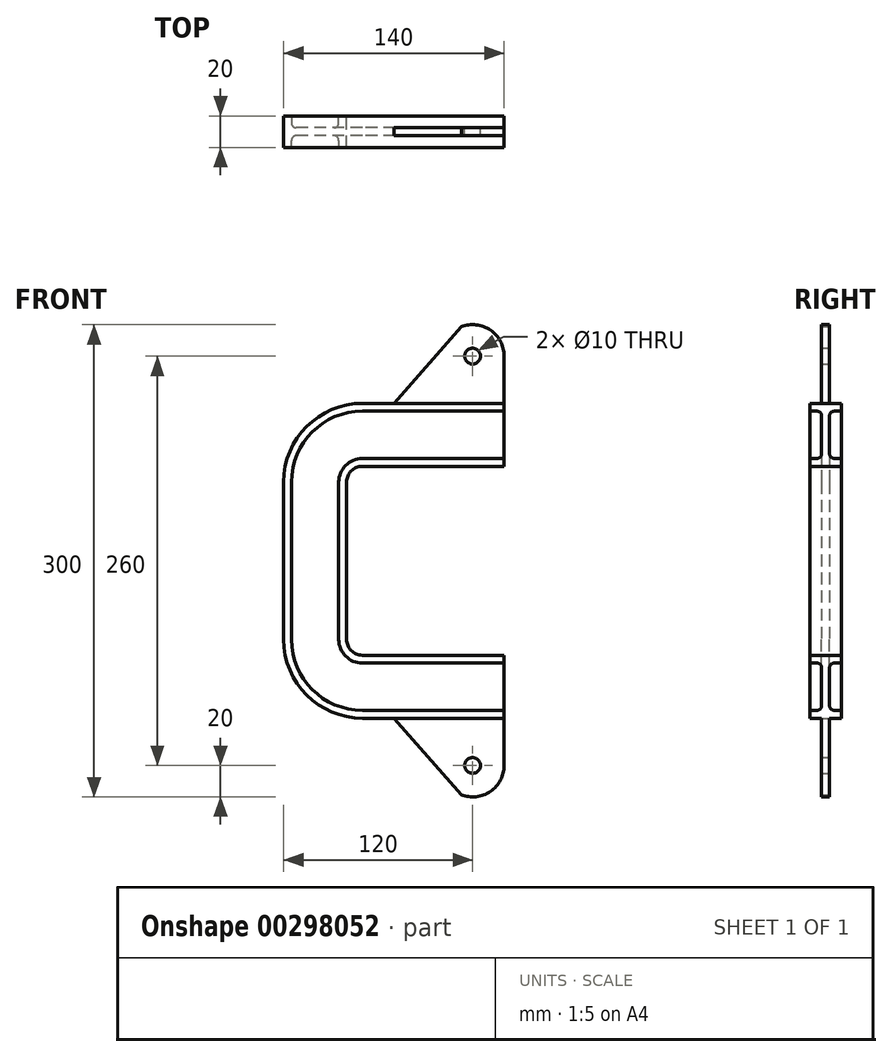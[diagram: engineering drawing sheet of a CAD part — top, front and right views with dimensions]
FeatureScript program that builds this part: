
annotation { "Feature Type Name" : "Feature", "Feature Type Description" : "" }
export const myFeature = defineFeature(function(context is Context, id is Id, definition is map)
    precondition{}
    {
        {
            var Q0;
            Q0=qCreatedBy(makeId("Front.planeOp"),FACE);
            var sketch = newSketch(context, id + "F0", { "sketchPlane" : qUnion([Q0])});
            skLineSegment(sketch, "E0", {"start": v(-100, 0) * mm, "end": v(-100, 50) * mm});
            skLineSegment(sketch, "E1", {"start": v(-90, 60) * mm, "end": v(0, 60) * mm});
            skPoint(sketch, "E2.visualSharp", {"position": v(-100, 60) * mm});
            skArc(sketch, "E2.filletArc", {"start": v(-90, 60) * mm, "mid": v(-97.07, 57.07) * mm, "end": v(-100, 50) * mm});
            skSolve(sketch);
        }
        {
            var Q0;
            Q0=qCreatedBy(makeId("Right.planeOp"),FACE);
            var sketch = newSketch(context, id + "F1", { "sketchPlane" : qUnion([Q0])});
            skLineSegment(sketch, "E3", {"start": v(0, 100) * mm, "end": v(10, 100) * mm});
            skLineSegment(sketch, "E4", {"start": v(10, 100) * mm, "end": v(10, 95) * mm});
            skLineSegment(sketch, "E5", {"start": v(10, 95) * mm, "end": v(5.5, 95) * mm});
            skLineSegment(sketch, "E6", {"start": v(2.5, 92) * mm, "end": v(2.5, 68) * mm});
            skLineSegment(sketch, "E7", {"start": v(5.5, 65) * mm, "end": v(10, 65) * mm});
            skLineSegment(sketch, "E8", {"start": v(10, 65) * mm, "end": v(10, 60) * mm});
            skLineSegment(sketch, "E9", {"start": v(10, 60) * mm, "end": v(0, 60) * mm});
            skPoint(sketch, "E10.visualSharp", {"position": v(2.5, 95) * mm});
            skArc(sketch, "E10.filletArc", {"start": v(5.5, 95) * mm, "mid": v(3.38, 94.12) * mm, "end": v(2.5, 92) * mm});
            skPoint(sketch, "E11.visualSharp", {"position": v(2.5, 65) * mm});
            skArc(sketch, "E11.filletArc", {"start": v(2.5, 68) * mm, "mid": v(3.38, 65.88) * mm, "end": v(5.5, 65) * mm});
            skLineSegment(sketch, "E12.MirrorCS", {"start": v(-5.5, 65) * mm, "end": v(-10, 65) * mm});
            skLineSegment(sketch, "E13.MirrorCS", {"start": v(-10, 95) * mm, "end": v(-5.5, 95) * mm});
            skArc(sketch, "E14.MirrorCS", {"start": v(-2.5, 68) * mm, "mid": v(-3.38, 65.88) * mm, "end": v(-5.5, 65) * mm});
            skArc(sketch, "E15.MirrorCS", {"start": v(-5.5, 95) * mm, "mid": v(-3.38, 94.12) * mm, "end": v(-2.5, 92) * mm});
            skLineSegment(sketch, "E16.MirrorCS", {"start": v(0, 100) * mm, "end": v(-10, 100) * mm});
            skLineSegment(sketch, "E17.MirrorCS", {"start": v(-10, 100) * mm, "end": v(-10, 95) * mm});
            skLineSegment(sketch, "E18.MirrorCS", {"start": v(-2.5, 92) * mm, "end": v(-2.5, 68) * mm});
            skLineSegment(sketch, "E19.MirrorCS", {"start": v(-10, 65) * mm, "end": v(-10, 60) * mm});
            skPoint(sketch, "E20.MirrorP", {"position": v(-2.5, 95) * mm});
            skLineSegment(sketch, "E21.MirrorCS", {"start": v(-10, 60) * mm, "end": v(0, 60) * mm});
            skPoint(sketch, "E22.MirrorP", {"position": v(-2.5, 65) * mm});
            skSolve(sketch);
        }
        {
            var Q0;
            Q0=makeQuery(id+"F1.imprint","IMPRINT",FACE,{"disambiguationData":[TD([[makeQuery(id+"F1.imprint","IMPRINT",EDGE,{"derivedFrom":sQuery(id+"F1.wireOp",EDGE,"E3")}),-1.0]])]});
            var Q1;
            Q1=sQuery(id+"F0.wireOp",EDGE,"E1");
            var Q2;
            Q2=sQuery(id+"F0.wireOp",EDGE,"E2.filletArc");
            var Q3;
            Q3=sQuery(id+"F0.wireOp",EDGE,"E0");
            sweep(context, id + "F2", {"profiles" : qUnion([Q0]), "path" : qUnion([Q1, Q2, Q3])});
        }
        {
            var Q0;
            Q0=makeQuery(id+"F2.opSweep","SWEPT_BODY",BODY,{"disambiguationData":[OSD([sQuery(id+"F0.wireOp",EDGE,"E0"),sQuery(id+"F1.wireOp",EDGE,"E3"),sQuery(id+"F1.wireOp",EDGE,"E4"),sQuery(id+"F1.wireOp",EDGE,"E5"),sQuery(id+"F1.wireOp",EDGE,"E6"),sQuery(id+"F1.wireOp",EDGE,"E7"),sQuery(id+"F1.wireOp",EDGE,"E8"),sQuery(id+"F1.wireOp",EDGE,"E9"),sQuery(id+"F1.wireOp",EDGE,"E10.filletArc"),sQuery(id+"F1.wireOp",EDGE,"E11.filletArc"),sQuery(id+"F1.wireOp",EDGE,"E12.MirrorCS"),sQuery(id+"F1.wireOp",EDGE,"E13.MirrorCS"),sQuery(id+"F1.wireOp",EDGE,"E14.MirrorCS"),sQuery(id+"F1.wireOp",EDGE,"E15.MirrorCS"),sQuery(id+"F1.wireOp",EDGE,"E16.MirrorCS"),sQuery(id+"F1.wireOp",EDGE,"E17.MirrorCS"),sQuery(id+"F1.wireOp",EDGE,"E18.MirrorCS"),sQuery(id+"F1.wireOp",EDGE,"E19.MirrorCS"),sQuery(id+"F1.wireOp",EDGE,"E21.MirrorCS")])]});
            var Q1;
            Q1=qCreatedBy(makeId("Top.planeOp"),FACE);
            mirror(context, id + "F3", {"operationType" : NewBodyOperationType.ADD, "entities" : qUnion([Q0]), "mirrorPlane" : qUnion([Q1])});
        }
        {
            var Q0;
            Q0=qCreatedBy(makeId("Front.planeOp"),FACE);
            var sketch = newSketch(context, id + "F4", { "sketchPlane" : qUnion([Q0])});
            skLineSegment(sketch, "E23", {"start": v(0, 100) * mm, "end": v(-70, 100) * mm});
            skLineSegment(sketch, "E24", {"start": v(0, 100) * mm, "end": v(0, 130) * mm});
            skLineSegment(sketch, "E25", {"start": v(-70, 100) * mm, "end": v(-27.19, 148.66) * mm});
            skArc(sketch, "E26", {"start": v(0, 130) * mm, "mid": v(-8.68, 146.49) * mm, "end": v(-27.19, 148.66) * mm});
            skCircle(sketch, "E27", {"center": v(-20, 130) * mm, "radius": 5 * mm});
            skLineSegment(sketch, "E28.MirrorCS", {"start": v(0, -100) * mm, "end": v(0, -130) * mm});
            skCircle(sketch, "E29.MirrorC", {"center": v(-20, -130) * mm, "radius": 5 * mm});
            skLineSegment(sketch, "E30.MirrorCS", {"start": v(-70, -100) * mm, "end": v(-27.19, -148.66) * mm});
            skLineSegment(sketch, "E31.MirrorCS", {"start": v(0, -100) * mm, "end": v(-70, -100) * mm});
            skArc(sketch, "E32.MirrorCS", {"start": v(0, -130) * mm, "mid": v(-8.68, -146.49) * mm, "end": v(-27.19, -148.66) * mm});
            skSolve(sketch);
        }
        {
            var Q0;
            Q0=makeQuery(id+"F4.imprint","IMPRINT",FACE,{"disambiguationData":[TD([[makeQuery(id+"F4.imprint","IMPRINT",EDGE,{"derivedFrom":sQuery(id+"F4.wireOp",EDGE,"E23")}),-1.0]])]});
            extrude(context, id + "F5", {"entities" : qUnion([Q0]), "endBound" : BoundingType.SYMMETRIC, "depth" : 5 * mm});
        }
        {
            var Q0;
            Q0=makeQuery(id+"F4.imprint","IMPRINT",FACE,{"disambiguationData":[TD([[makeQuery(id+"F4.imprint","IMPRINT",EDGE,{"derivedFrom":sQuery(id+"F4.wireOp",EDGE,"E28.MirrorCS")}),-1.0]])]});
            extrude(context, id + "F6", {"entities" : qUnion([Q0]), "operationType" : NewBodyOperationType.ADD, "endBound" : BoundingType.SYMMETRIC, "depth" : 5 * mm});
        }
    });
